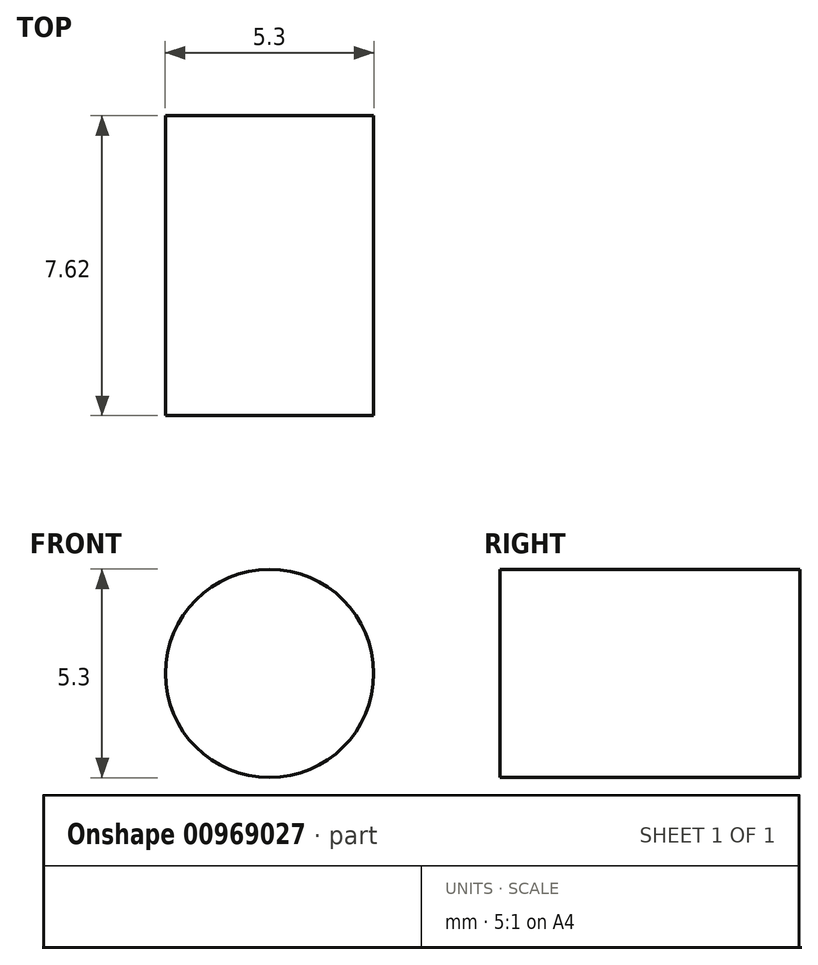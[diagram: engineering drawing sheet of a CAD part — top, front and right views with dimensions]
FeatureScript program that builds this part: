
annotation { "Feature Type Name" : "Feature", "Feature Type Description" : "" }
export const myFeature = defineFeature(function(context is Context, id is Id, definition is map)
    precondition{}
    {
        {
            var Q0;
            Q0=qCreatedBy(makeId("Front.planeOp"),FACE);
            var sketch = newSketch(context, id + "F0", { "sketchPlane" : qUnion([Q0])});
            skCircle(sketch, "E0", {"center": v(0, 0) * mm, "radius": 2.65 * mm});
            skSolve(sketch);
        }
        {
            var Q0;
            Q0 = qSketchRegion(id + "F0", true);
            extrude(context, id + "F1", {"entities" : qUnion([Q0]), "depth" : 7.62 * mm, "offsetDistance" : 25.4 * mm});
        }
    });
